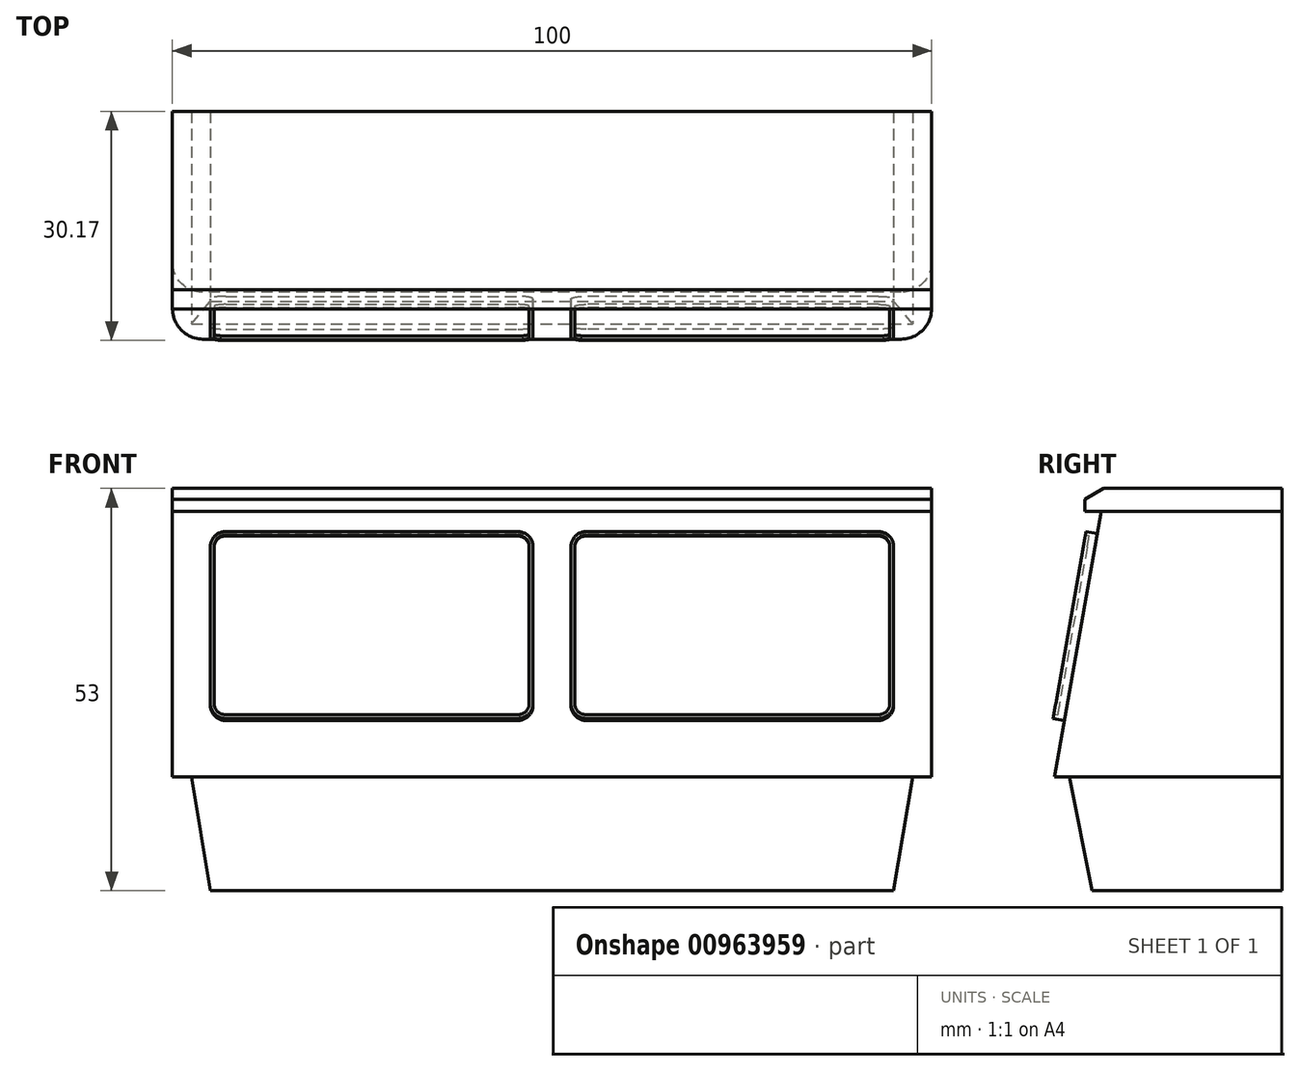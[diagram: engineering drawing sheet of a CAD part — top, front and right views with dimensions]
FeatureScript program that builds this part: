
annotation { "Feature Type Name" : "Feature", "Feature Type Description" : "" }
export const myFeature = defineFeature(function(context is Context, id is Id, definition is map)
    precondition{}
    {
        {
            var Q0;
            Q0=qCreatedBy(makeId("Right.planeOp"),FACE);
            var sketch = newSketch(context, id + "F0", { "sketchPlane" : qUnion([Q0])});
            skLineSegment(sketch, "E0", {"start": v(0, 0) * mm, "end": v(0, 35) * mm});
            skLineSegment(sketch, "E1", {"start": v(0, 35) * mm, "end": v(-23.83, 35) * mm});
            skLineSegment(sketch, "E2", {"start": v(-23.83, 35) * mm, "end": v(-30, 0) * mm});
            skLineSegment(sketch, "E3", {"start": v(-30, 0) * mm, "end": v(0, 0) * mm});
            skSolve(sketch);
        }
        {
            var Q0;
            Q0 = qSketchRegion(id + "F0", true);
            extrude(context, id + "F1", {"entities" : qUnion([Q0]), "endBound" : BoundingType.SYMMETRIC, "depth" : 100 * mm, "offsetDistance" : 25 * mm});
        }
        {
            var Q0;
            Q0=qCreatedBy(makeId("Right.planeOp"),FACE);
            var sketch = newSketch(context, id + "F2", { "sketchPlane" : qUnion([Q0])});
            skLineSegment(sketch, "E4", {"start": v(0, 38) * mm, "end": v(-23.5, 38) * mm});
            skLineSegment(sketch, "E5", {"start": v(-26, 35) * mm, "end": v(0, 35) * mm});
            skLineSegment(sketch, "E6", {"start": v(0, 35) * mm, "end": v(0, 38) * mm});
            skLineSegment(sketch, "E7", {"start": v(-23.5, 38) * mm, "end": v(-26, 36.56) * mm});
            skLineSegment(sketch, "E8", {"start": v(-26, 36.56) * mm, "end": v(-26, 35) * mm});
            skSolve(sketch);
        }
        {
            var Q0;
            Q0 = qSketchRegion(id + "F2", true);
            extrude(context, id + "F3", {"entities" : qUnion([Q0]), "endBound" : BoundingType.SYMMETRIC, "depth" : 100 * mm, "offsetDistance" : 25 * mm});
        }
        {
            var Q0;
            Q0=makeQuery(id+"F1.opExtrude","SWEPT_FACE",FACE,{"disambiguationData":[OSD([sQuery(id+"F0.wireOp",EDGE,"E3")])]});
            var sketch = newSketch(context, id + "F4", { "sketchPlane" : qUnion([Q0])});
            skLineSegment(sketch, "E9.bottom", {"start": v(-47.5, 0) * mm, "end": v(47.5, 0) * mm});
            skLineSegment(sketch, "E9.top", {"start": v(-47.5, 28) * mm, "end": v(47.5, 28) * mm});
            skLineSegment(sketch, "E9.left", {"start": v(-47.5, 0) * mm, "end": v(-47.5, 28) * mm});
            skLineSegment(sketch, "E9.right", {"start": v(47.5, 0) * mm, "end": v(47.5, 28) * mm});
            skSolve(sketch);
        }
        {
            var Q0;
            Q0=qCreatedBy(makeId("Top.planeOp"),FACE);
            cPlane(context, id + "F5", {"entities" : qUnion([Q0]), "cplaneType" : CPlaneType.OFFSET, "offset" : 15 * mm, "oppositeDirection" : true, "width" : 150 * mm, "height" : 150 * mm});
        }
        {
            var Q0;
            Q0=qCreatedBy(id+"F5.planeOp",FACE);
            var sketch = newSketch(context, id + "F6", { "sketchPlane" : qUnion([Q0])});
            skLineSegment(sketch, "E10.bottom", {"start": v(-45, 0) * mm, "end": v(45, 0) * mm});
            skLineSegment(sketch, "E10.top", {"start": v(-45, -25) * mm, "end": v(45, -25) * mm});
            skLineSegment(sketch, "E10.left", {"start": v(-45, 0) * mm, "end": v(-45, -25) * mm});
            skLineSegment(sketch, "E10.right", {"start": v(45, 0) * mm, "end": v(45, -25) * mm});
            skSolve(sketch);
        }
        {
            var Q1;
            Q1 = qSketchRegion(id + "F4", true);
            var Q2;
            Q2 = qSketchRegion(id + "F6", true);
            loft(context, id + "F7", {"sheetProfilesArray" : [{ "sheetProfileEntities" : qUnion([Q1]) }, { "sheetProfileEntities" : qUnion([Q2]) }]});
        }
        {
            var Q0;
            Q0=makeQuery(id+"F1.opExtrude","SWEPT_FACE",FACE,{"disambiguationData":[OSD([sQuery(id+"F0.wireOp",EDGE,"E2")])]});
            var sketch = newSketch(context, id + "F8", { "sketchPlane" : qUnion([Q0])});
            skLineSegment(sketch, "E11.bottom", {"start": v(-43, 27.33) * mm, "end": v(-4.5, 27.33) * mm});
            skLineSegment(sketch, "E11.top", {"start": v(-43, 2.33) * mm, "end": v(-4.5, 2.33) * mm});
            skLineSegment(sketch, "E11.left", {"start": v(-45, 25.33) * mm, "end": v(-45, 4.33) * mm});
            skLineSegment(sketch, "E11.right", {"start": v(-2.5, 25.33) * mm, "end": v(-2.5, 4.33) * mm});
            skPoint(sketch, "E12.visualSharp", {"position": v(-45, 27.33) * mm});
            skArc(sketch, "E12.filletArc", {"start": v(-43, 27.33) * mm, "mid": v(-44.41, 26.74) * mm, "end": v(-45, 25.33) * mm});
            skPoint(sketch, "E13.visualSharp", {"position": v(-45, 2.33) * mm});
            skArc(sketch, "E13.filletArc", {"start": v(-45, 4.33) * mm, "mid": v(-44.41, 2.92) * mm, "end": v(-43, 2.33) * mm});
            skPoint(sketch, "E14.visualSharp", {"position": v(-2.5, 2.33) * mm});
            skArc(sketch, "E14.filletArc", {"start": v(-4.5, 2.33) * mm, "mid": v(-3.09, 2.92) * mm, "end": v(-2.5, 4.33) * mm});
            skPoint(sketch, "E15.visualSharp", {"position": v(-2.5, 27.33) * mm});
            skArc(sketch, "E15.filletArc", {"start": v(-2.5, 25.33) * mm, "mid": v(-3.09, 26.74) * mm, "end": v(-4.5, 27.33) * mm});
            skSolve(sketch);
        }
        {
            var Q0;
            Q0 = qSketchRegion(id + "F8", true);
            extrude(context, id + "F9", {"entities" : qUnion([Q0]), "depth" : 1.5 * mm, "offsetDistance" : 25 * mm});
        }
        {
            var Q0;
            Q0=makeQuery(id+"F9.opExtrude","CAP_FACE",FACE,{"disambiguationData":[OSD([sQuery(id+"F8.wireOp",EDGE,"E11.bottom"),sQuery(id+"F8.wireOp",EDGE,"E11.top"),sQuery(id+"F8.wireOp",EDGE,"E11.left"),sQuery(id+"F8.wireOp",EDGE,"E11.right"),sQuery(id+"F8.wireOp",EDGE,"E12.filletArc"),sQuery(id+"F8.wireOp",EDGE,"E13.filletArc"),sQuery(id+"F8.wireOp",EDGE,"E14.filletArc"),sQuery(id+"F8.wireOp",EDGE,"E15.filletArc")])],"isStart":false});
            var sketch = newSketch(context, id + "F10", { "sketchPlane" : qUnion([Q0])});
            skLineSegment(sketch, "E16.bottom", {"start": v(-44, 27.33) * mm, "end": v(-3.5, 27.33) * mm, "construction": true});
            skLineSegment(sketch, "E16.top", {"start": v(-44, 2.33) * mm, "end": v(-3.5, 2.33) * mm, "construction": true});
            skLineSegment(sketch, "E16.left", {"start": v(-45, 26.33) * mm, "end": v(-45, 3.33) * mm, "construction": true});
            skLineSegment(sketch, "E16.right", {"start": v(-2.5, 26.33) * mm, "end": v(-2.5, 3.33) * mm, "construction": true});
            skPoint(sketch, "E17.visualSharp", {"position": v(-45, 27.33) * mm});
            skArc(sketch, "E17.filletArc", {"start": v(-44, 27.33) * mm, "mid": v(-44.7, 27.04) * mm, "end": v(-45, 26.33) * mm, "construction": true});
            skPoint(sketch, "E18.visualSharp", {"position": v(-45, 2.33) * mm});
            skArc(sketch, "E18.filletArc", {"start": v(-45, 3.33) * mm, "mid": v(-44.7, 2.62) * mm, "end": v(-44, 2.33) * mm, "construction": true});
            skPoint(sketch, "E19.visualSharp", {"position": v(-2.5, 2.33) * mm});
            skArc(sketch, "E19.filletArc", {"start": v(-3.5, 2.33) * mm, "mid": v(-2.8, 2.62) * mm, "end": v(-2.5, 3.33) * mm, "construction": true});
            skPoint(sketch, "E20.visualSharp", {"position": v(-2.5, 27.33) * mm});
            skArc(sketch, "E20.filletArc", {"start": v(-2.5, 26.33) * mm, "mid": v(-2.8, 27.04) * mm, "end": v(-3.5, 27.33) * mm, "construction": true});
            skLineSegment(sketch, "E21.0", {"start": v(-44.5, 25.33) * mm, "end": v(-44.5, 4.33) * mm});
            skLineSegment(sketch, "E21.1", {"start": v(-43, 26.83) * mm, "end": v(-4.5, 26.83) * mm});
            skLineSegment(sketch, "E21.2", {"start": v(-3, 25.33) * mm, "end": v(-3, 4.33) * mm});
            skLineSegment(sketch, "E21.3", {"start": v(-43, 2.83) * mm, "end": v(-4.5, 2.83) * mm});
            skPoint(sketch, "E22.visualSharp", {"position": v(-44.5, 26.83) * mm});
            skArc(sketch, "E22.filletArc", {"start": v(-43, 26.83) * mm, "mid": v(-44.06, 26.4) * mm, "end": v(-44.5, 25.33) * mm});
            skPoint(sketch, "E23.visualSharp", {"position": v(-3, 26.83) * mm});
            skArc(sketch, "E23.filletArc", {"start": v(-3, 25.33) * mm, "mid": v(-3.44, 26.4) * mm, "end": v(-4.5, 26.83) * mm});
            skPoint(sketch, "E24.visualSharp", {"position": v(-3, 2.83) * mm});
            skArc(sketch, "E24.filletArc", {"start": v(-4.5, 2.83) * mm, "mid": v(-3.44, 3.27) * mm, "end": v(-3, 4.33) * mm});
            skPoint(sketch, "E25.visualSharp", {"position": v(-44.5, 2.83) * mm});
            skArc(sketch, "E25.filletArc", {"start": v(-44.5, 4.33) * mm, "mid": v(-44.06, 3.27) * mm, "end": v(-43, 2.83) * mm});
            skSolve(sketch);
        }
        {
            var Q0;
            Q0 = qSketchRegion(id + "F10", true);
            extrude(context, id + "F11", {"entities" : qUnion([Q0]), "operationType" : NewBodyOperationType.REMOVE, "oppositeDirection" : true, "depth" : .5 * mm, "offsetDistance" : 25 * mm});
        }
        {
            var Q0;
            Q0=makeQuery(id+"F9.opExtrude","SWEPT_BODY",BODY,{"disambiguationData":[OSD([sQuery(id+"F8.wireOp",EDGE,"E11.bottom"),sQuery(id+"F8.wireOp",EDGE,"E11.top"),sQuery(id+"F8.wireOp",EDGE,"E11.left"),sQuery(id+"F8.wireOp",EDGE,"E11.right"),sQuery(id+"F8.wireOp",EDGE,"E12.filletArc"),sQuery(id+"F8.wireOp",EDGE,"E13.filletArc"),sQuery(id+"F8.wireOp",EDGE,"E14.filletArc"),sQuery(id+"F8.wireOp",EDGE,"E15.filletArc")])]});
            var Q1;
            Q1=qCreatedBy(makeId("Right.planeOp"),FACE);
            mirror(context, id + "F12", {"entities" : qUnion([Q0]), "mirrorPlane" : qUnion([Q1])});
        }
        {
            var Q0;
            Q0=makeQuery(id+"F1.opExtrude","CAP_EDGE",EDGE,{"disambiguationData":[OSD([sQuery(id+"F0.wireOp",EDGE,"E2")])],"isStart":true});
            var Q1;
            Q1=makeQuery(id+"F1.opExtrude","CAP_EDGE",EDGE,{"disambiguationData":[OSD([sQuery(id+"F0.wireOp",EDGE,"E2")])],"isStart":false});
            fillet(context, id + "F13", {"entities" : qUnion([Q0, Q1]), "radius" : 4 * mm, "tangentPropagation" : true, "allowEdgeOverflow" : false});
        }
    });
